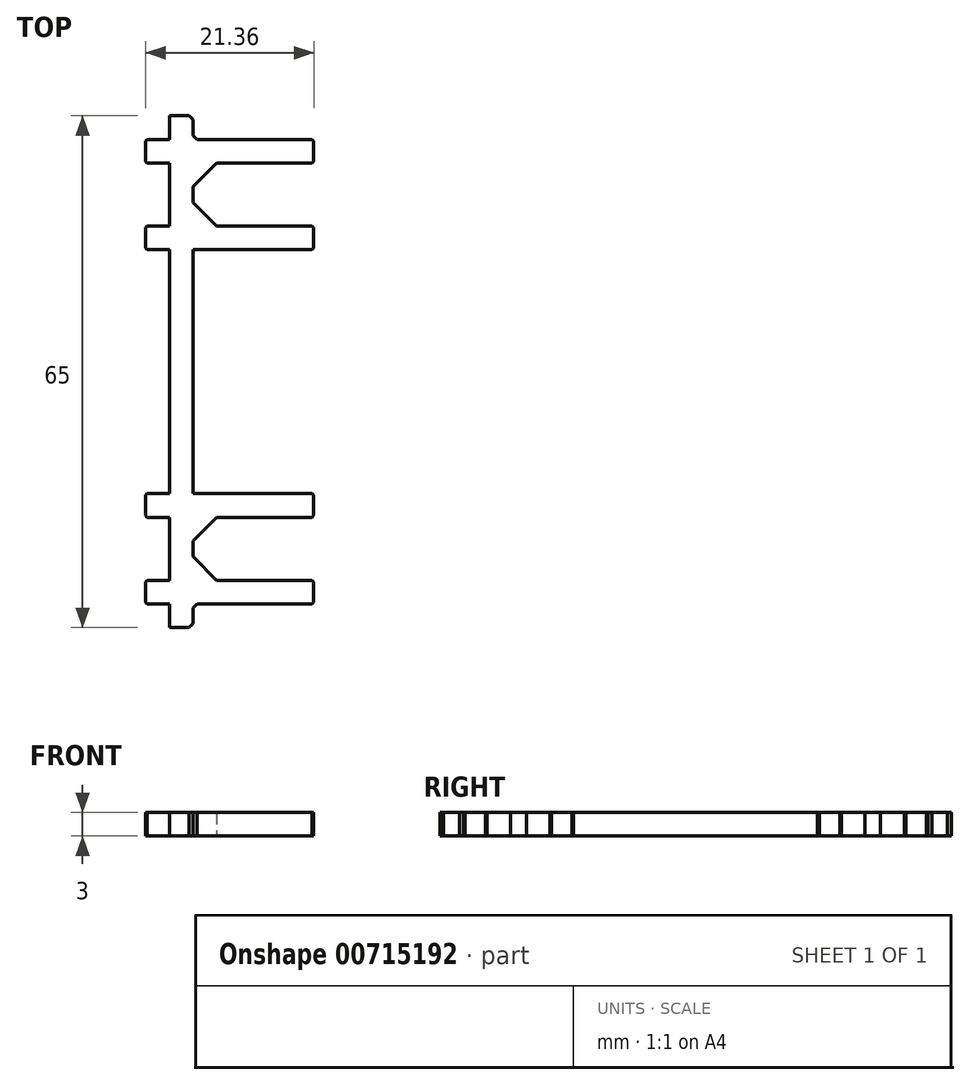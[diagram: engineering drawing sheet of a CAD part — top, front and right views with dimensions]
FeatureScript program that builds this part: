
annotation { "Feature Type Name" : "Feature", "Feature Type Description" : "" }
export const myFeature = defineFeature(function(context is Context, id is Id, definition is map)
    precondition{}
    {
        {
            var Q0;
            Q0=qCreatedBy(makeId("Top.planeOp"),FACE);
            var sketch = newSketch(context, id + "F0", { "sketchPlane" : qUnion([Q0])});
            skLineSegment(sketch, "E0", {"start": v(-1.68, 26.5) * mm, "end": v(-4.67, 23.5) * mm});
            skLineSegment(sketch, "E1", {"start": v(-4.68, 21.5) * mm, "end": v(-1.68, 18.5) * mm});
            skLineSegment(sketch, "E2", {"start": v(-1.68, -18.5) * mm, "end": v(-4.68, -21.5) * mm});
            skLineSegment(sketch, "E3", {"start": v(-4.68, -23.5) * mm, "end": v(-1.68, -26.5) * mm});
            skLineSegment(sketch, "E4", {"start": v(-4.68, 23.5) * mm, "end": v(-4.68, 21.5) * mm});
            skLineSegment(sketch, "E5", {"start": v(-4.68, -21.5) * mm, "end": v(-4.68, -23.5) * mm});
            skLineSegment(sketch, "E6", {"start": v(-7.68, 26.5) * mm, "end": v(-7.68, 18.5) * mm});
            skLineSegment(sketch, "E7", {"start": v(-7.68, 15.5) * mm, "end": v(-7.68, -15.5) * mm});
            skLineSegment(sketch, "E8", {"start": v(-7.68, -18.5) * mm, "end": v(-7.68, -26.5) * mm});
            skLineSegment(sketch, "E9", {"start": v(-7.68, 29.5) * mm, "end": v(-7.68, 32.5) * mm});
            skLineSegment(sketch, "E10", {"start": v(-7.68, -29.5) * mm, "end": v(-7.68, -32.5) * mm});
            skLineSegment(sketch, "E11", {"start": v(-4.68, 15.5) * mm, "end": v(-4.68, -15.5) * mm});
            skLineSegment(sketch, "E12", {"start": v(-7.68, 32.5) * mm, "end": v(-5.17, 32.5) * mm});
            skLineSegment(sketch, "E13", {"start": v(-4.68, 32) * mm, "end": v(-5.17, 32.5) * mm});
            skLineSegment(sketch, "E14", {"start": v(-7.68, -32.5) * mm, "end": v(-5.17, -32.5) * mm});
            skLineSegment(sketch, "E15", {"start": v(-5.17, -32.5) * mm, "end": v(-4.68, -32) * mm});
            skLineSegment(sketch, "E16", {"start": v(-4.68, 32) * mm, "end": v(-4.68, 30) * mm});
            skLineSegment(sketch, "E17", {"start": v(-4.68, 30) * mm, "end": v(-4.17, 29.5) * mm});
            skLineSegment(sketch, "E18", {"start": v(-4.68, -30) * mm, "end": v(-4.68, -32) * mm});
            skLineSegment(sketch, "E19", {"start": v(-4.68, -30) * mm, "end": v(-4.17, -29.5) * mm});
            skLineSegment(sketch, "E20", {"start": v(-4.17, 29.5) * mm, "end": v(10.47, 29.5) * mm});
            skLineSegment(sketch, "E21", {"start": v(10.47, 29.5) * mm, "end": v(10.68, 29.3) * mm});
            skLineSegment(sketch, "E22", {"start": v(10.68, 29.3) * mm, "end": v(10.68, 26.7) * mm});
            skLineSegment(sketch, "E23", {"start": v(-1.68, 26.5) * mm, "end": v(10.47, 26.5) * mm});
            skLineSegment(sketch, "E24", {"start": v(10.68, 26.7) * mm, "end": v(10.47, 26.5) * mm});
            skLineSegment(sketch, "E25", {"start": v(-1.68, 18.5) * mm, "end": v(10.47, 18.5) * mm});
            skLineSegment(sketch, "E26", {"start": v(10.47, 18.5) * mm, "end": v(10.68, 18.3) * mm});
            skLineSegment(sketch, "E27", {"start": v(10.68, 18.3) * mm, "end": v(10.68, 15.7) * mm});
            skLineSegment(sketch, "E28", {"start": v(10.47, 15.5) * mm, "end": v(-4.68, 15.5) * mm});
            skLineSegment(sketch, "E29", {"start": v(10.68, 15.7) * mm, "end": v(10.47, 15.5) * mm});
            skLineSegment(sketch, "E30", {"start": v(10.47, -15.5) * mm, "end": v(-4.68, -15.5) * mm});
            skLineSegment(sketch, "E31", {"start": v(10.47, -15.5) * mm, "end": v(10.68, -15.7) * mm});
            skLineSegment(sketch, "E32", {"start": v(10.68, -15.7) * mm, "end": v(10.68, -18.3) * mm});
            skLineSegment(sketch, "E33", {"start": v(-1.68, -18.5) * mm, "end": v(10.47, -18.5) * mm});
            skLineSegment(sketch, "E34", {"start": v(10.68, -18.3) * mm, "end": v(10.47, -18.5) * mm});
            skLineSegment(sketch, "E35", {"start": v(10.47, -26.5) * mm, "end": v(-1.67, -26.5) * mm});
            skLineSegment(sketch, "E36", {"start": v(10.47, -26.5) * mm, "end": v(10.68, -26.7) * mm});
            skLineSegment(sketch, "E37", {"start": v(10.68, -26.7) * mm, "end": v(10.68, -29.3) * mm});
            skLineSegment(sketch, "E38", {"start": v(-4.17, -29.5) * mm, "end": v(10.47, -29.5) * mm});
            skLineSegment(sketch, "E39", {"start": v(10.68, -29.3) * mm, "end": v(10.47, -29.5) * mm});
            skLineSegment(sketch, "E40", {"start": v(-10.47, 29.5) * mm, "end": v(-7.68, 29.5) * mm});
            skLineSegment(sketch, "E41", {"start": v(-10.47, 29.5) * mm, "end": v(-10.67, 29.3) * mm});
            skLineSegment(sketch, "E42", {"start": v(-10.67, 29.3) * mm, "end": v(-10.67, 26.7) * mm});
            skLineSegment(sketch, "E43", {"start": v(-10.47, 26.5) * mm, "end": v(-7.68, 26.5) * mm});
            skLineSegment(sketch, "E44", {"start": v(-10.67, 26.7) * mm, "end": v(-10.47, 26.5) * mm});
            skLineSegment(sketch, "E45", {"start": v(-7.68, 18.5) * mm, "end": v(-10.47, 18.5) * mm});
            skLineSegment(sketch, "E46", {"start": v(-10.47, 18.5) * mm, "end": v(-10.67, 18.3) * mm});
            skLineSegment(sketch, "E47", {"start": v(-10.67, 18.3) * mm, "end": v(-10.67, 15.7) * mm});
            skLineSegment(sketch, "E48", {"start": v(-10.47, 15.5) * mm, "end": v(-7.68, 15.5) * mm});
            skLineSegment(sketch, "E49", {"start": v(-10.67, 15.7) * mm, "end": v(-10.47, 15.5) * mm});
            skLineSegment(sketch, "E50", {"start": v(-7.68, -15.5) * mm, "end": v(-10.47, -15.5) * mm});
            skLineSegment(sketch, "E51", {"start": v(-10.47, -15.5) * mm, "end": v(-10.67, -15.7) * mm});
            skLineSegment(sketch, "E52", {"start": v(-10.67, -15.7) * mm, "end": v(-10.67, -18.3) * mm});
            skLineSegment(sketch, "E53", {"start": v(-10.47, -18.5) * mm, "end": v(-7.68, -18.5) * mm});
            skLineSegment(sketch, "E54", {"start": v(-10.67, -18.3) * mm, "end": v(-10.47, -18.5) * mm});
            skLineSegment(sketch, "E55", {"start": v(-7.68, -26.5) * mm, "end": v(-10.47, -26.5) * mm});
            skLineSegment(sketch, "E56", {"start": v(-10.47, -26.5) * mm, "end": v(-10.67, -26.7) * mm});
            skLineSegment(sketch, "E57", {"start": v(-10.67, -26.7) * mm, "end": v(-10.67, -29.3) * mm});
            skLineSegment(sketch, "E58", {"start": v(-10.47, -29.5) * mm, "end": v(-7.68, -29.5) * mm});
            skLineSegment(sketch, "E59", {"start": v(-10.67, -29.3) * mm, "end": v(-10.47, -29.5) * mm});
            skSolve(sketch);
        }
        {
            var Q0;
            Q0 = qSketchRegion(id + "F0", true);
            extrude(context, id + "F1", {"entities" : qUnion([Q0]), "depth" : 3 * mm, "offsetDistance" : 25 * mm});
        }
    });
